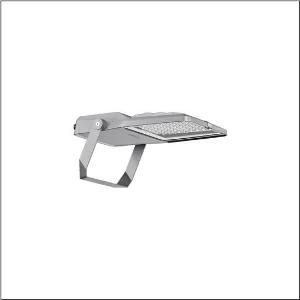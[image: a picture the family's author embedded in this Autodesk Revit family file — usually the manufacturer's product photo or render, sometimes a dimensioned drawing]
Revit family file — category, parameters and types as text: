
# Revit family: floodlight_fl_21_mini___pl52_5xa7773c2d1a_dd61
name_source: partatom
category: Lighting Fixtures
units: mm (PartAtom-declared; Revit-internal decimal feet)

## family parameters
Cut with Voids When Loaded = No
Host = Face
Light Source = No
Part Type = Normal
Room Calculation Point = No
Round Connector Dimension = Use Diameter
Shared = No

## types (1)
- --- (1 x LED, 19510 lm, 163.5 W, 3000K)
    Apparent Load = 163 VA
    CIE Flux Codes = 26 60 98 100 100
    Color Rendering = 70
    Color Temperature = 3000K
    Default Elevation = 1800 mm
    Description = Floodlight FL 21 mini, floodlight, primary light control with lens, of PMMA, primary optical cover: protective disc, of toughened safety glass, transparent, light distribution: PL52, light emission: direct distribution, installation type: surface-mounted, LED, High Power LED, rated luminous flux: 19.510lm, luminous efficacy: 119lm/W, light colour: 730, colour temperature: 3000K, control: Temp-Guard, with terminal, 6-pole, mains connection: 220..240V, AC, 50/60Hz, start of lifetime: 164W, luminaire housing, of diecast aluminium, powder-coated, Siteco® metallic grey (DB 702S), corrosivity category C5 mid according to DIN EN ISO 12944, sealing non-destructively replaceable, mounting bracket, of steel, galvanised, powder-coated, Siteco® metallic grey (DB 702S), ON/OFF, protection rating (complete): IP66, insulation class (complete): insulation class I (protective earthing), certification: CE, ENEC, VDE, protection symbol: D, impact resistance: IK08, permissible operating ambient temperature: -40..+40°C, permissible operating ambient temperature for outdoor applications: -40..+50°C, standard: DIN EN 12944, LABS conformity tested according to VDMA 24364:2018-05, packaging unit: 1 piece

Light Distribution: PL52
    Height = 70 mm
    Lamp = 1 x LED
    Lamp Light Flux = 19510 lm
    Lamp Power = 163.5 W
    Lamp count = 1
    Length = 485 mm
    Luminous efficacy = 119 lm/W
    Manufacturer = Siteco
    ModVariant = No
    Model = 5XA7773C2D1A
    Number of Poles = 1
    OnlyDefault = Yes
    Power Factor = 1
    Product Name = Floodlight FL 21 mini | PL52
    Product group = floodlight | pylon annexe
    ProductGroupID = 6200
    Protection Class = Protection class I
    Protection Degree = IP 66
    RLX_Detail_Level = 1
    RLX_Emergency_Light_Flux = 0 lm
    RLX_Emergency_Type = 0
    RLX_Emergency_Type_DB = No
    RlxData = <blob elided: 94421 chars, md5=c71135d2>
    Socket = socket
    Standby Power = 0 W
    System Light Flux = 19510 lm
    System Power = 163 W
    Type Comments = factory setting: luminous flux: 100 % | (ON | - | - | - | - | - | - | -) | 825 mA
    Type Image = l_1006845.jpg
    URL = http://relux.com
    VarID = @adj_114259
    Voltage = 0 V
    Weight = 0.00 kg
    Width = 337 mm

## geometry (parser evidence)
native form markers: Blend x4, Sweep x14
no freeform markers — native parametric forms only
